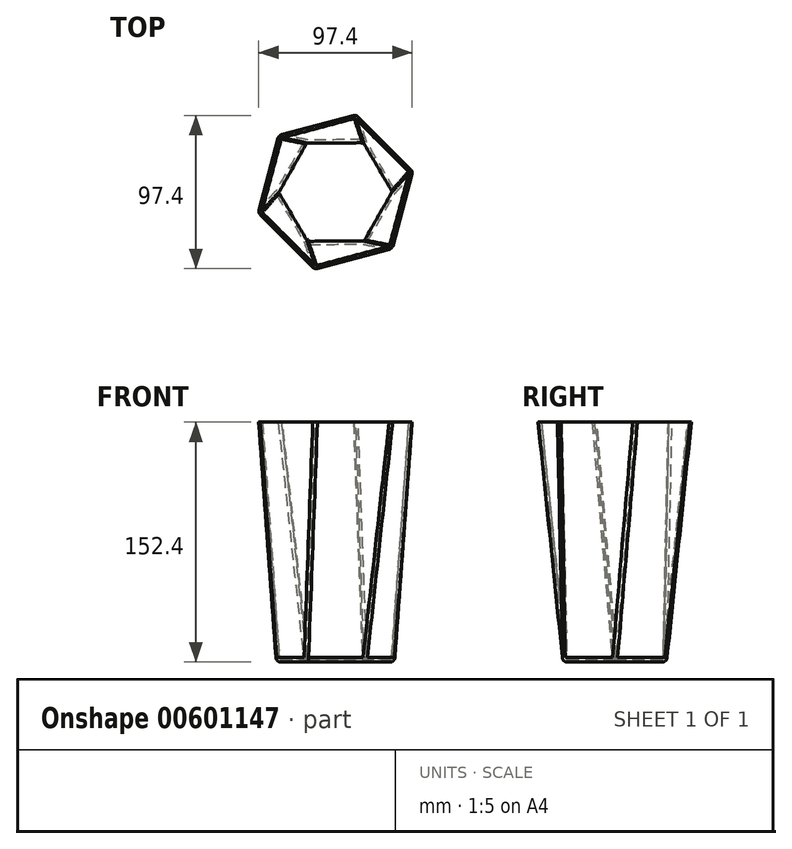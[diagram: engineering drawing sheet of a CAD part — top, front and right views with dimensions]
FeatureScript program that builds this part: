
annotation { "Feature Type Name" : "Feature", "Feature Type Description" : "" }
export const myFeature = defineFeature(function(context is Context, id is Id, definition is map)
    precondition{}
    {
        {
            var Q0;
            Q0=qCreatedBy(makeId("Top.planeOp"),FACE);
            var sketch = newSketch(context, id + "F0", { "sketchPlane" : qUnion([Q0])});
            skCircle(sketch, "E0.cCircle", {"center": v(0, 0) * mm, "radius": 33 * mm, "construction": true});
            skLineSegment(sketch, "E0.0", {"start": v(38.1, 0) * mm, "end": v(19.05, -33) * mm});
            skLineSegment(sketch, "E0.1", {"start": v(19.05, -33) * mm, "end": v(-19.05, -33) * mm});
            skLineSegment(sketch, "E0.2", {"start": v(-19.05, -33) * mm, "end": v(-38.1, 0) * mm});
            skLineSegment(sketch, "E0.3", {"start": v(-38.1, 0) * mm, "end": v(-19.05, 33) * mm});
            skLineSegment(sketch, "E0.4", {"start": v(-19.05, 33) * mm, "end": v(19.05, 33) * mm});
            skLineSegment(sketch, "E0.5", {"start": v(19.05, 33) * mm, "end": v(38.1, 0) * mm});
            skPoint(sketch, "E0.0.midPoint", {"position": v(28.57, -16.5) * mm});
            skSolve(sketch);
        }
        {
            var Q0;
            Q0=qCreatedBy(makeId("Top.planeOp"),FACE);
            cPlane(context, id + "F1", {"entities" : qUnion([Q0]), "cplaneType" : CPlaneType.OFFSET, "offset" : 152.4 * mm, "width" : 152.4 * mm, "height" : 152.4 * mm});
        }
        {
            var Q0;
            Q0=qCreatedBy(id+"F1.planeOp",FACE);
            var sketch = newSketch(context, id + "F2", { "sketchPlane" : qUnion([Q0])});
            skCircle(sketch, "E1.cCircle", {"center": v(0, 0) * mm, "radius": 44 * mm, "construction": true});
            skLineSegment(sketch, "E1.0", {"start": v(49.07, 13.15) * mm, "end": v(13.15, 49.07) * mm});
            skLineSegment(sketch, "E1.1", {"start": v(35.92, -35.92) * mm, "end": v(49.07, 13.15) * mm});
            skLineSegment(sketch, "E1.2", {"start": v(-13.15, -49.07) * mm, "end": v(35.92, -35.92) * mm});
            skLineSegment(sketch, "E1.3", {"start": v(-49.07, -13.15) * mm, "end": v(-13.15, -49.07) * mm});
            skLineSegment(sketch, "E1.4", {"start": v(-35.92, 35.92) * mm, "end": v(-49.07, -13.15) * mm});
            skLineSegment(sketch, "E1.5", {"start": v(13.15, 49.07) * mm, "end": v(-35.92, 35.92) * mm});
            skPoint(sketch, "E1.0.midPoint", {"position": v(31.1, 31.1) * mm});
            skSolve(sketch);
        }
        {
            var Q0;
            Q0=makeQuery(id+"F0.imprint","IMPRINT",FACE,{"disambiguationData":[TD([[makeQuery(id+"F0.imprint","IMPRINT",EDGE,{"derivedFrom":sQuery(id+"F0.wireOp",EDGE,"E0.0")}),-1.0]])]});
            var Q1;
            Q1=makeQuery(id+"F2.imprint","IMPRINT",FACE,{"disambiguationData":[TD([[makeQuery(id+"F2.imprint","IMPRINT",EDGE,{"derivedFrom":sQuery(id+"F2.wireOp",EDGE,"E1.0")}),1.0]])]});
            var Q2;
            Q2=sQuery(id+"F2.wireOp",VERTEX,"E1.3.end");
            var Q3;
            Q3=sQuery(id+"F0.wireOp",VERTEX,"E0.2.start");
            loft(context, id + "F3", {"sheetProfilesArray" : [{ "sheetProfileEntities" : qUnion([Q0]) }, { "sheetProfileEntities" : qUnion([Q1]) }], "matchConnections" : true, "connections" : [{ "connectionEntities" : qUnion([Q2, Q3]), "connectionEdgeQueries" : qUnion([]), "connectionEdgeParameters" : [] }]});
        }
        {
            var Q0;
            Q0=makeQuery(id+"F3.opLoft","MID_CAP_EDGE",EDGE,{"disambiguationData":[OSD([sQuery(id+"F0.wireOp",EDGE,"E0.0"),sQuery(id+"F0.wireOp",EDGE,"E0.1"),sQuery(id+"F0.wireOp",EDGE,"E0.2")])],"capPos":0.0});
            var Q1;
            Q1=makeQuery(id+"F3.opLoft","MID_CAP_EDGE",EDGE,{"disambiguationData":[OSD([sQuery(id+"F0.wireOp",EDGE,"E0.0"),sQuery(id+"F0.wireOp",EDGE,"E0.1"),sQuery(id+"F0.wireOp",EDGE,"E0.5")])],"capPos":0.0});
            var Q2;
            Q2=makeQuery(id+"F3.opLoft","MID_CAP_EDGE",EDGE,{"disambiguationData":[OSD([sQuery(id+"F0.wireOp",EDGE,"E0.0"),sQuery(id+"F0.wireOp",EDGE,"E0.4"),sQuery(id+"F0.wireOp",EDGE,"E0.5")])],"capPos":0.0});
            var Q3;
            Q3=makeQuery(id+"F3.opLoft","MID_CAP_EDGE",EDGE,{"disambiguationData":[OSD([sQuery(id+"F0.wireOp",EDGE,"E0.3"),sQuery(id+"F0.wireOp",EDGE,"E0.4"),sQuery(id+"F0.wireOp",EDGE,"E0.5")])],"capPos":0.0});
            var Q4;
            Q4=makeQuery(id+"F3.opLoft","MID_CAP_EDGE",EDGE,{"disambiguationData":[OSD([sQuery(id+"F0.wireOp",EDGE,"E0.2"),sQuery(id+"F0.wireOp",EDGE,"E0.3"),sQuery(id+"F0.wireOp",EDGE,"E0.4")])],"capPos":0.0});
            var Q5;
            Q5=makeQuery(id+"F3.opLoft","MID_CAP_EDGE",EDGE,{"disambiguationData":[OSD([sQuery(id+"F0.wireOp",EDGE,"E0.1"),sQuery(id+"F0.wireOp",EDGE,"E0.2"),sQuery(id+"F0.wireOp",EDGE,"E0.3")])],"capPos":0.0});
            var Q6;
            Q6=makeQuery(id+"F3.opLoft","SWEPT_EDGE",EDGE,{"disambiguationData":[OSD([sQuery(id+"F0.wireOp",EDGE,"E0.0"),sQuery(id+"F0.wireOp",EDGE,"E0.5"),sQuery(id+"F2.wireOp",EDGE,"E1.1"),sQuery(id+"F2.wireOp",EDGE,"E1.2")])]});
            var Q7;
            Q7=makeQuery(id+"F3.opLoft","SWEPT_EDGE",EDGE,{"disambiguationData":[OSD([sQuery(id+"F0.wireOp",EDGE,"E0.4"),sQuery(id+"F0.wireOp",EDGE,"E0.5"),sQuery(id+"F2.wireOp",EDGE,"E1.0"),sQuery(id+"F2.wireOp",EDGE,"E1.1")])]});
            var Q8;
            Q8=makeQuery(id+"F3.opLoft","SWEPT_EDGE",EDGE,{"disambiguationData":[OSD([sQuery(id+"F0.wireOp",EDGE,"E0.3"),sQuery(id+"F0.wireOp",EDGE,"E0.4"),sQuery(id+"F2.wireOp",EDGE,"E1.0"),sQuery(id+"F2.wireOp",EDGE,"E1.5")])]});
            var Q9;
            Q9=makeQuery(id+"F3.opLoft","SWEPT_EDGE",EDGE,{"disambiguationData":[OSD([sQuery(id+"F0.wireOp",EDGE,"E0.2"),sQuery(id+"F0.wireOp",EDGE,"E0.3"),sQuery(id+"F2.wireOp",EDGE,"E1.4"),sQuery(id+"F2.wireOp",EDGE,"E1.5")])]});
            var Q10;
            Q10=makeQuery(id+"F3.opLoft","SWEPT_EDGE",EDGE,{"disambiguationData":[OSD([sQuery(id+"F0.wireOp",EDGE,"E0.1"),sQuery(id+"F0.wireOp",EDGE,"E0.2"),sQuery(id+"F2.wireOp",EDGE,"E1.3"),sQuery(id+"F2.wireOp",EDGE,"E1.4")])]});
            var Q11;
            Q11=makeQuery(id+"F3.opLoft","SWEPT_EDGE",EDGE,{"disambiguationData":[OSD([sQuery(id+"F0.wireOp",EDGE,"E0.0"),sQuery(id+"F0.wireOp",EDGE,"E0.1"),sQuery(id+"F2.wireOp",EDGE,"E1.2"),sQuery(id+"F2.wireOp",EDGE,"E1.3")])]});
            fillet(context, id + "F4", {"entities" : qUnion([Q0, Q1, Q2, Q3, Q4, Q5, Q6, Q7, Q8, Q9, Q10, Q11]), "radius" : 3.17 * mm, "tangentPropagation" : true, "allowEdgeOverflow" : false});
        }
        {
            var Q0;
            Q0=makeQuery(id+"F3.opLoft","CAP_FACE",FACE,{"disambiguationData":[OSD([makeQuery(id+"F2.imprint","IMPRINT",FACE,{"disambiguationData":[TD([[makeQuery(id+"F2.imprint","IMPRINT",EDGE,{"derivedFrom":sQuery(id+"F2.wireOp",EDGE,"E1.0")}),1.0]])]})])],"isStart":true});
            shell(context, id + "F5", {"entities" : qUnion([Q0]), "thickness" : 2 * mm});
        }
    });
